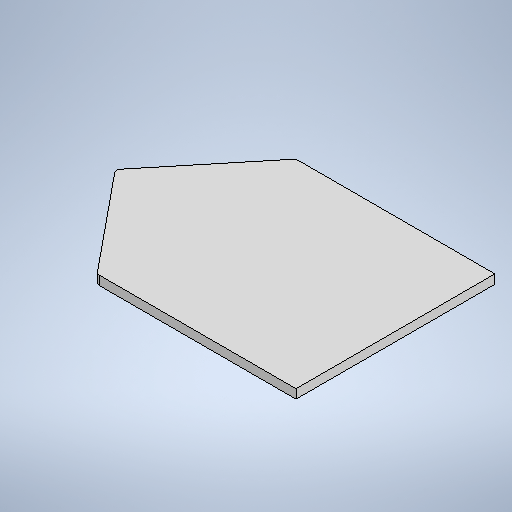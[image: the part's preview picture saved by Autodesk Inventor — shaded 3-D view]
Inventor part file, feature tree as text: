
AUTODESK INVENTOR PART (.ipt)
format: ipt  version: 2025 (Build 290162010, 162A)  size: 232,960 bytes
history: native  units: mm
features: sheet_metal_op x1, chamfer x1, sketch x1, other x1
ambient origin geometry x8: Origin, YZ Plane, XZ Plane, XY Plane, X Axis, Y Axis, Z Axis, Center Point
bodies: Solid1 (feature_tree)
feature tree (4):
  sheet_metal_op  "Face1"
  chamfer  "Corner Round2"
  sketch  "Sketch1"  dims[d0=44.0mm d1=44.0mm d2=2.0mm d4=62.0mm d6=1.0mm]
  other  "Plate1"
